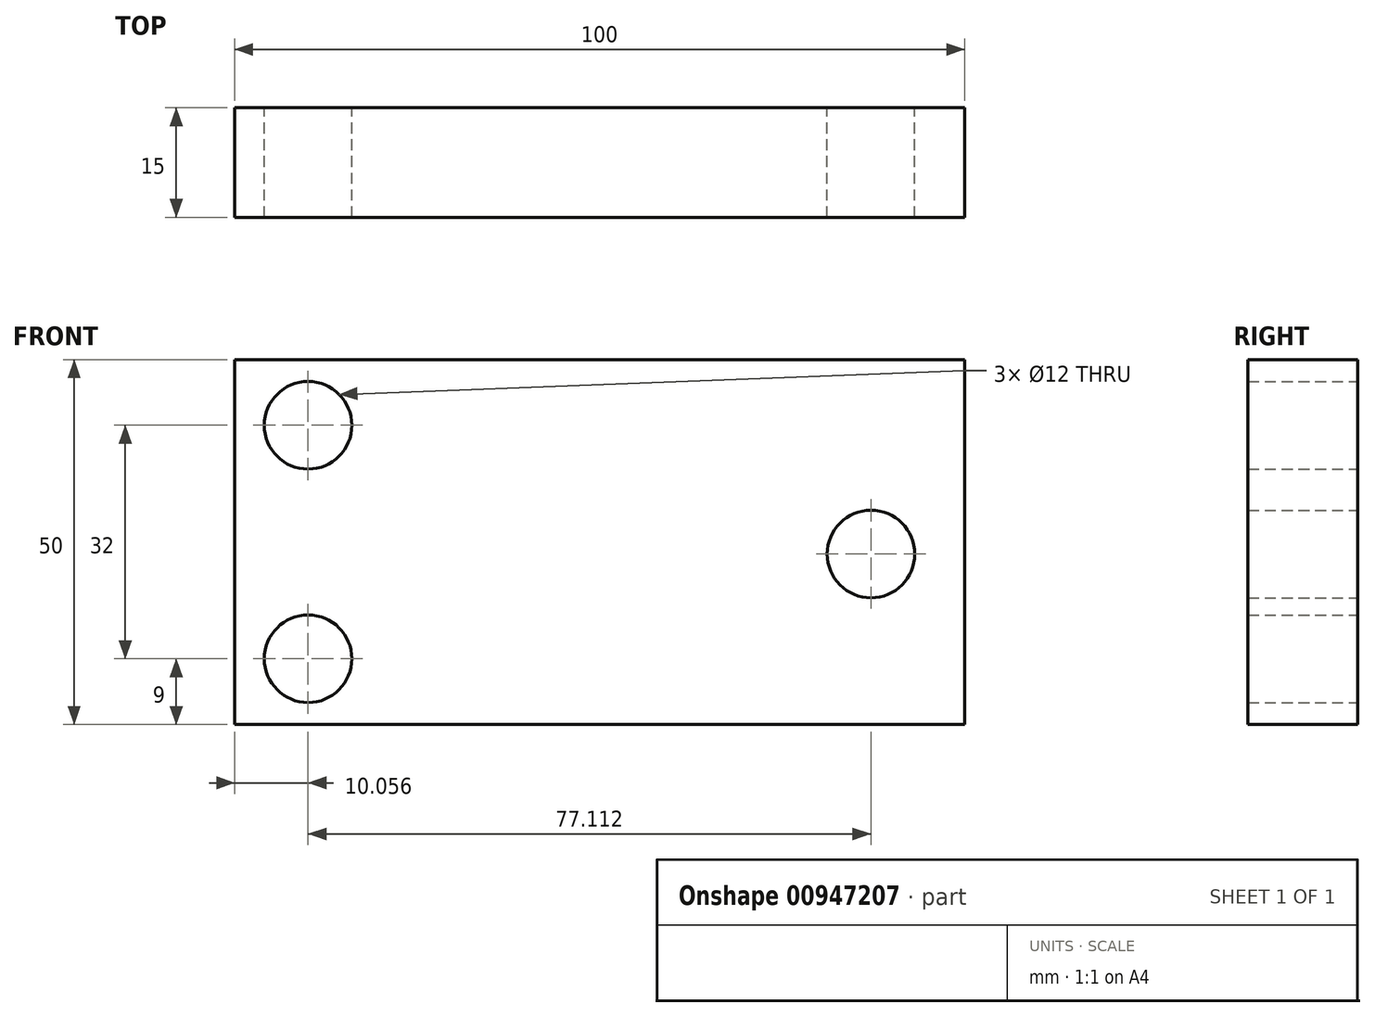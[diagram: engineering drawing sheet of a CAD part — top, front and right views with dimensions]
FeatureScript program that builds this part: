
annotation { "Feature Type Name" : "Feature", "Feature Type Description" : "" }
export const myFeature = defineFeature(function(context is Context, id is Id, definition is map)
    precondition{}
    {
        {
            var Q0;
            Q0=qCreatedBy(makeId("Front.planeOp"),FACE);
            var sketch = newSketch(context, id + "F0", { "sketchPlane" : qUnion([Q0])});
            skLineSegment(sketch, "E0.bottom", {"start": v(-50, 0) * mm, "end": v(50, 0) * mm});
            skLineSegment(sketch, "E0.top", {"start": v(-50, 50) * mm, "end": v(50, 50) * mm});
            skLineSegment(sketch, "E0.left", {"start": v(-50, 0) * mm, "end": v(-50, 50) * mm});
            skLineSegment(sketch, "E0.right", {"start": v(50, 0) * mm, "end": v(50, 50) * mm});
            skCircle(sketch, "E1", {"center": v(-39.94, 41) * mm, "radius": 6 * mm});
            skCircle(sketch, "E2.MirrorC", {"center": v(-39.94, 9) * mm, "radius": 6 * mm});
            skCircle(sketch, "E3", {"center": v(37.17, 23.35) * mm, "radius": 6 * mm});
            skSolve(sketch);
        }
        {
            var Q0;
            Q0 = qSketchRegion(id + "F0", true);
            extrude(context, id + "F1", {"entities" : qUnion([Q0]), "depth" : 15 * mm, "offsetDistance" : 25 * mm});
        }
    });
